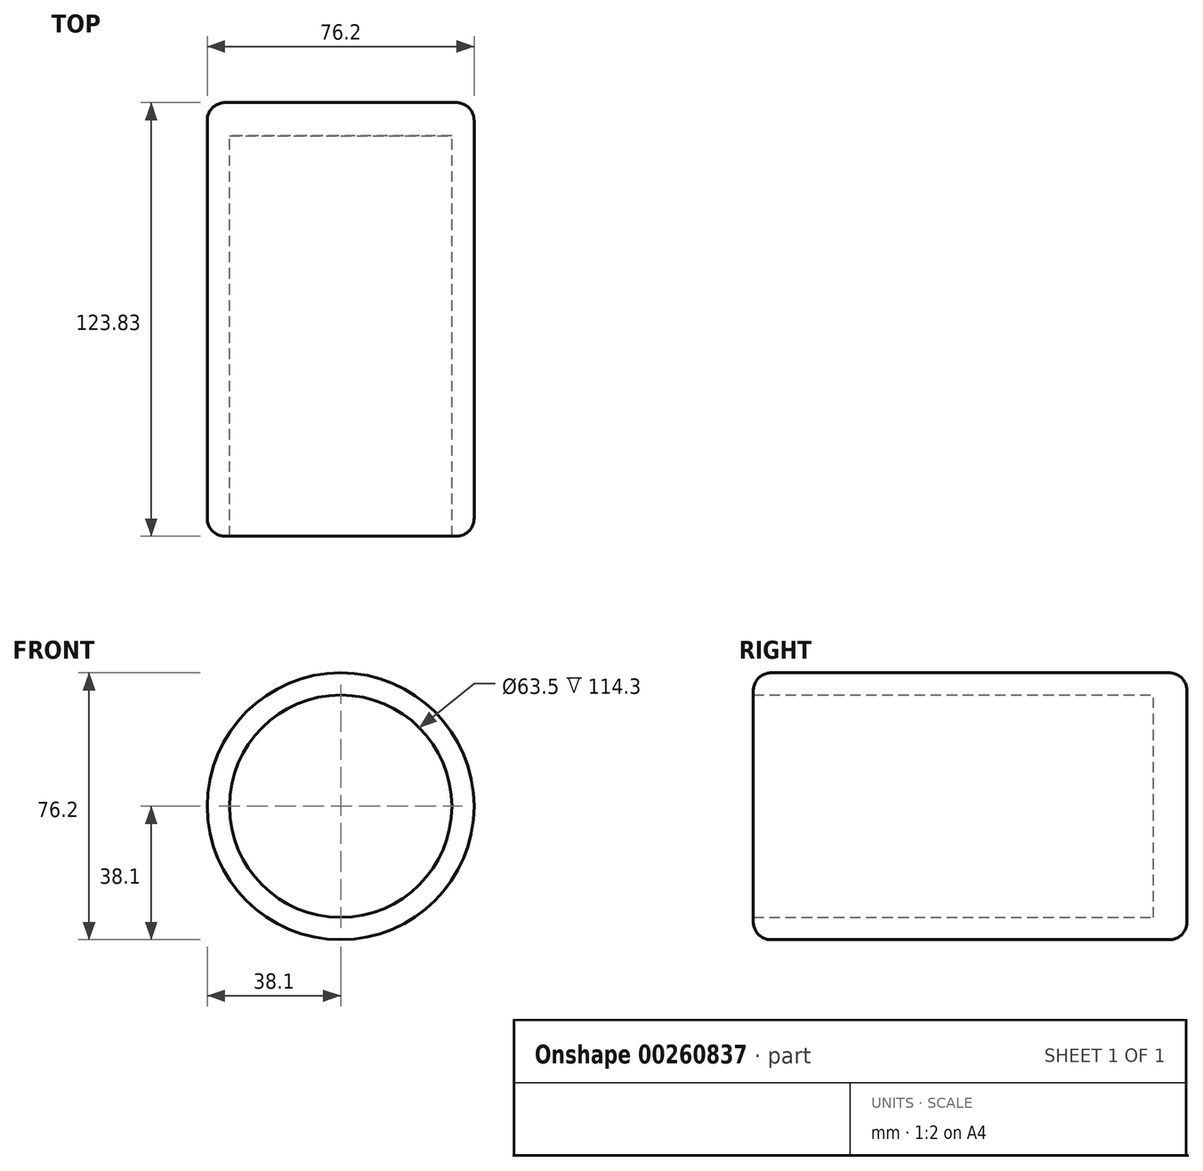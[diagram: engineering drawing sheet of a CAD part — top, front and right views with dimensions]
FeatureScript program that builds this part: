
annotation { "Feature Type Name" : "Feature", "Feature Type Description" : "" }
export const myFeature = defineFeature(function(context is Context, id is Id, definition is map)
    precondition{}
    {
        {
            var Q0;
            Q0=qCreatedBy(makeId("Front.planeOp"),FACE);
            var sketch = newSketch(context, id + "F0", { "sketchPlane" : qUnion([Q0])});
            skCircle(sketch, "E0", {"center": v(0, 0) * mm, "radius": 38.1 * mm});
            skCircle(sketch, "E1", {"center": v(0, 0) * mm, "radius": 31.75 * mm});
            skSolve(sketch);
        }
        {
            var Q0;
            Q0=makeQuery(id+"F0.imprint","IMPRINT",FACE,{"disambiguationData":[TD([[makeQuery(id+"F0.imprint","IMPRINT",EDGE,{"derivedFrom":sQuery(id+"F0.wireOp",EDGE,"E0")}),1.0]])]});
            extrude(context, id + "F1", {"entities" : qUnion([Q0]), "depth" : 123.82 * mm});
        }
        {
            var Q0;
            Q0=qCreatedBy(makeId("Front.planeOp"),FACE);
            var sketch = newSketch(context, id + "F2", { "sketchPlane" : qUnion([Q0])});
            skCircle(sketch, "E2", {"center": v(0, 0) * mm, "radius": 31.75 * mm});
            skSolve(sketch);
        }
        {
            var Q0;
            Q0=makeQuery(id+"F2.imprint","IMPRINT",FACE,{"disambiguationData":[TD([[makeQuery(id+"F2.imprint","IMPRINT",EDGE,{"derivedFrom":sQuery(id+"F2.wireOp",EDGE,"E2")}),1.0]])]});
            extrude(context, id + "F3", {"entities" : qUnion([Q0]), "operationType" : NewBodyOperationType.ADD, "depth" : 9.52 * mm});
        }
        {
            var Q0;
            Q0=makeQuery(id+"F1.opExtrude","CAP_EDGE",EDGE,{"disambiguationData":[OSD([sQuery(id+"F0.wireOp",EDGE,"E0")])],"isStart":false});
            var Q1;
            Q1=makeQuery(id+"F1.opExtrude","SWEPT_FACE",FACE,{"disambiguationData":[OSD([sQuery(id+"F0.wireOp",EDGE,"E0")])]});
            fillet(context, id + "F4", {"entities" : qUnion([Q0, Q1]), "radius" : 5.08 * mm, "tangentPropagation" : true, "allowEdgeOverflow" : false});
        }
    });
